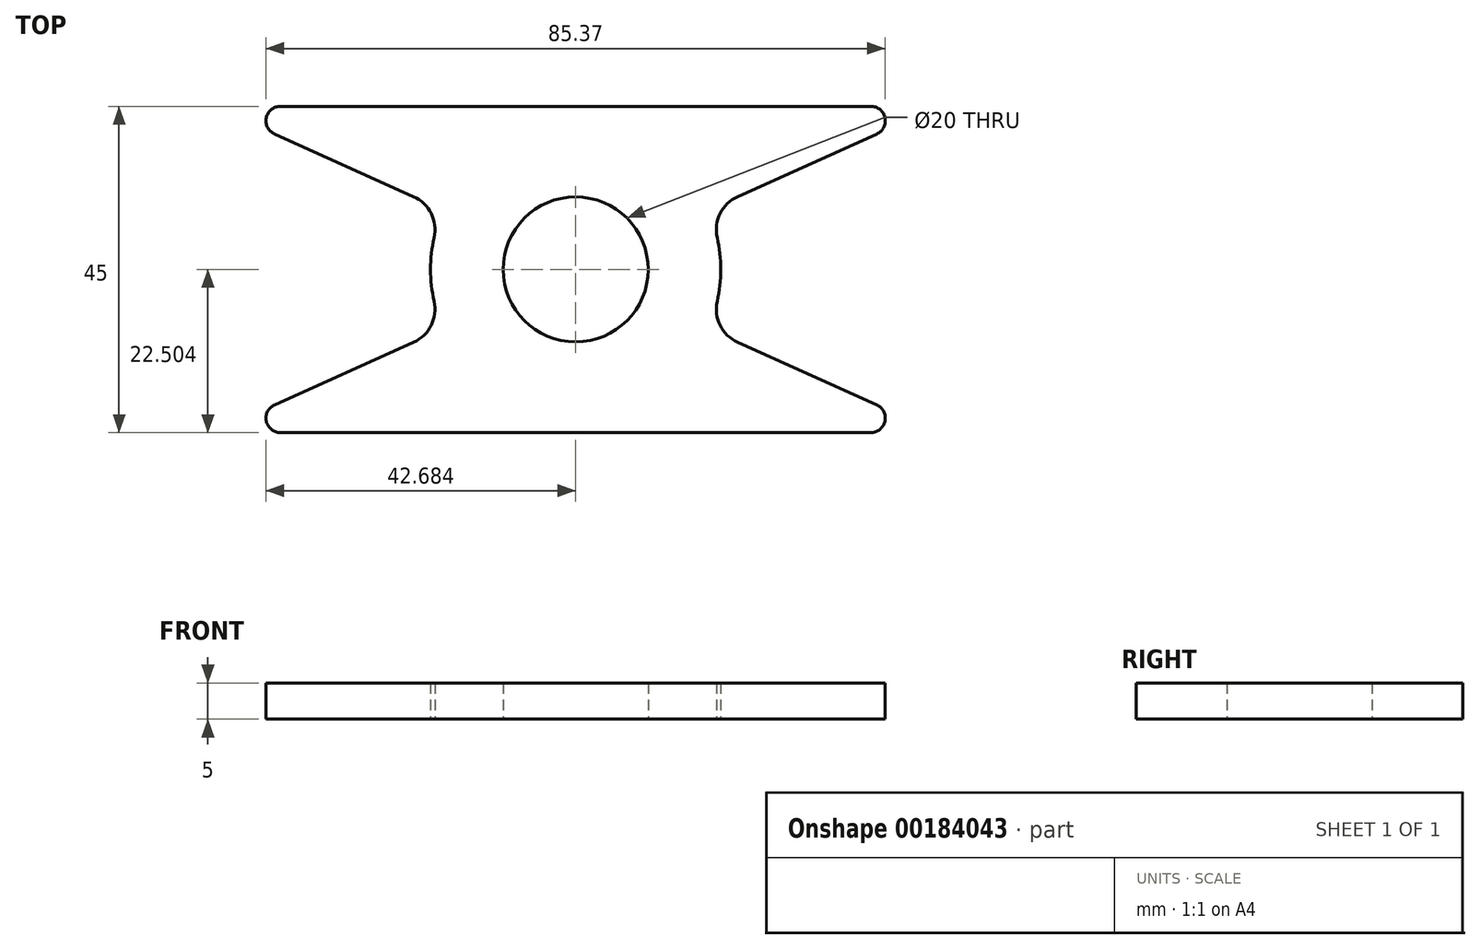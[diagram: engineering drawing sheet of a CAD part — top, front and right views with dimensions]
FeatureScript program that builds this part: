
annotation { "Feature Type Name" : "Feature", "Feature Type Description" : "" }
export const myFeature = defineFeature(function(context is Context, id is Id, definition is map)
    precondition{}
    {
        {
            var Q0;
            Q0=qCreatedBy(makeId("Top.planeOp"),FACE);
            var sketch = newSketch(context, id + "F0", { "sketchPlane" : qUnion([Q0])});
            skLineSegment(sketch, "E0.bottom", {"start": v(-43.45, 29.23) * mm, "end": v(56.55, 29.23) * mm});
            skLineSegment(sketch, "E0.top", {"start": v(-43.45, -15.77) * mm, "end": v(56.55, -15.77) * mm});
            skLineSegment(sketch, "E1", {"start": v(-43.45, 29.23) * mm, "end": v(-11.68, 14.94) * mm});
            skLineSegment(sketch, "E2", {"start": v(56.55, 29.23) * mm, "end": v(24.8, 14.94) * mm});
            skCircle(sketch, "E3", {"center": v(6.55, 6.73) * mm, "radius": 20 * mm});
            skLineSegment(sketch, "E4.trimOffspring", {"start": v(24.8, -1.47) * mm, "end": v(56.55, -15.77) * mm});
            skLineSegment(sketch, "E5.trimOffspring", {"start": v(-11.68, -1.47) * mm, "end": v(-43.45, -15.77) * mm});
            skCircle(sketch, "E6", {"center": v(6.55, 6.73) * mm, "radius": 10 * mm});
            skSolve(sketch);
        }
        {
            var Q0;
            {var subQ0=sQuery(id+"F0.wireOp",EDGE,"E3");var subQ1=makeQuery(id+"F0.imprint","INTERSECT",VERTEX,{"derivedFrom":[sQuery(id+"F0.wireOp",EDGE,"E1"),subQ0]});Q0=makeQuery(id+"F0.imprint","IMPRINT",FACE,{"disambiguationData":[TD([[makeQuery(id+"F0.imprint","IMPRINT",EDGE,{"disambiguationData":[TD([[subQ1,1.0]])],"derivedFrom":subQ0}),1.0]])]});}
            var Q1;
            Q1=makeQuery(id+"F0.imprint","IMPRINT",FACE,{"disambiguationData":[TD([[makeQuery(id+"F0.imprint","IMPRINT",EDGE,{"derivedFrom":sQuery(id+"F0.wireOp",EDGE,"E0.bottom")}),-1.0]])]});
            var Q2;
            Q2=makeQuery(id+"F0.imprint","IMPRINT",FACE,{"disambiguationData":[TD([[makeQuery(id+"F0.imprint","IMPRINT",EDGE,{"derivedFrom":sQuery(id+"F0.wireOp",EDGE,"E0.top")}),1.0]])]});
            extrude(context, id + "F1", {"entities" : qUnion([Q0, Q1, Q2]), "depth" : 5 * mm});
        }
        {
            var Q0;
            Q0=makeQuery(id+"F1.opExtrude","SWEPT_EDGE",EDGE,{"disambiguationData":[OSD([sQuery(id+"F0.wireOp",EDGE,"E0.bottom"),sQuery(id+"F0.wireOp",EDGE,"E1")])]});
            var Q1;
            Q1=makeQuery(id+"F1.opExtrude","SWEPT_EDGE",EDGE,{"disambiguationData":[OSD([sQuery(id+"F0.wireOp",EDGE,"E0.top"),sQuery(id+"F0.wireOp",EDGE,"E5.trimOffspring")])]});
            var Q2;
            Q2=makeQuery(id+"F1.opExtrude","SWEPT_EDGE",EDGE,{"disambiguationData":[OSD([sQuery(id+"F0.wireOp",EDGE,"E0.top"),sQuery(id+"F0.wireOp",EDGE,"E4.trimOffspring")])]});
            var Q3;
            Q3=makeQuery(id+"F1.opExtrude","SWEPT_EDGE",EDGE,{"disambiguationData":[OSD([sQuery(id+"F0.wireOp",EDGE,"E0.bottom"),sQuery(id+"F0.wireOp",EDGE,"E2")])]});
            fillet(context, id + "F2", {"entities" : qUnion([Q0, Q1, Q2, Q3]), "radius" : 2 * mm, "tangentPropagation" : true, "allowEdgeOverflow" : false});
        }
        {
            var Q0;
            Q0=makeQuery(id+"F1.opExtrude","SWEPT_EDGE",EDGE,{"disambiguationData":[OSD([sQuery(id+"F0.wireOp",EDGE,"E2"),sQuery(id+"F0.wireOp",EDGE,"E3")])]});
            var Q1;
            Q1=makeQuery(id+"F1.opExtrude","SWEPT_EDGE",EDGE,{"disambiguationData":[OSD([sQuery(id+"F0.wireOp",EDGE,"E3"),sQuery(id+"F0.wireOp",EDGE,"E4.trimOffspring")])]});
            var Q2;
            Q2=makeQuery(id+"F1.opExtrude","SWEPT_EDGE",EDGE,{"disambiguationData":[OSD([sQuery(id+"F0.wireOp",EDGE,"E3"),sQuery(id+"F0.wireOp",EDGE,"E5.trimOffspring")])]});
            var Q3;
            Q3=makeQuery(id+"F1.opExtrude","SWEPT_EDGE",EDGE,{"disambiguationData":[OSD([sQuery(id+"F0.wireOp",EDGE,"E1"),sQuery(id+"F0.wireOp",EDGE,"E3")])]});
            fillet(context, id + "F3", {"entities" : qUnion([Q0, Q1, Q2, Q3]), "radius" : 5 * mm, "tangentPropagation" : true, "allowEdgeOverflow" : false});
        }
    });
